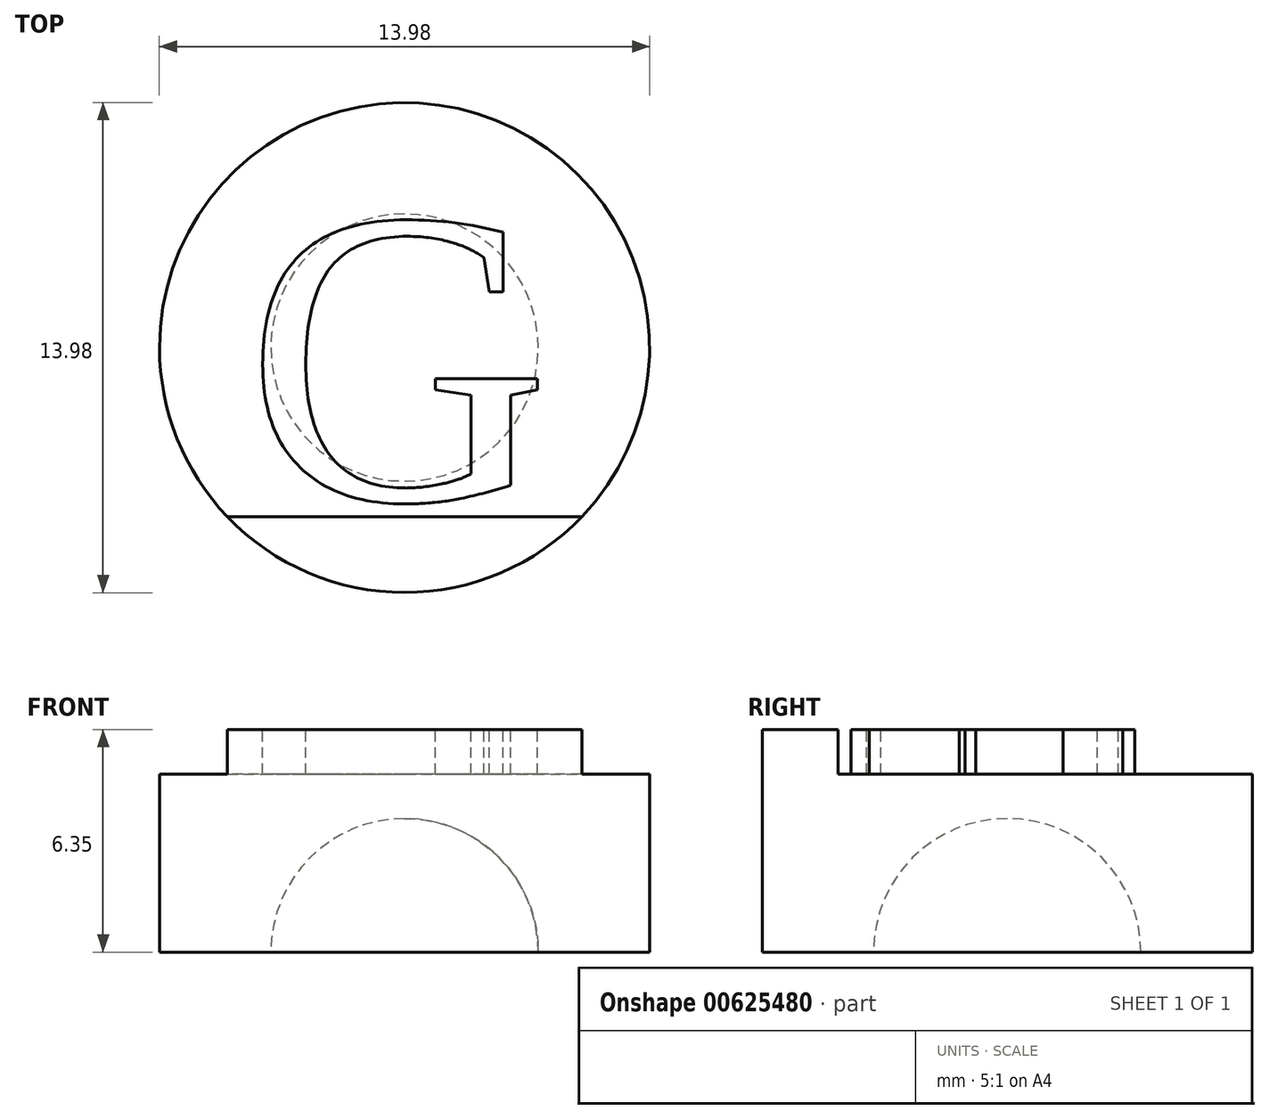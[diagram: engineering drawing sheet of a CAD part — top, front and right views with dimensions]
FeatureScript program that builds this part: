
annotation { "Feature Type Name" : "Feature", "Feature Type Description" : "" }
export const myFeature = defineFeature(function(context is Context, id is Id, definition is map)
    precondition{}
    {
        {
            var Q0;
            Q0=qCreatedBy(makeId("Front.planeOp"),FACE);
            var sketch = newSketch(context, id + "F0", { "sketchPlane" : qUnion([Q0])});
            skLineSegment(sketch, "E0", {"start": v(-6.99, 0) * mm, "end": v(-3.8, 0) * mm});
            skLineSegment(sketch, "E1", {"start": v(0, 3.81) * mm, "end": v(0, 6.35) * mm});
            skLineSegment(sketch, "E2", {"start": v(0, 6.35) * mm, "end": v(-6.99, 6.35) * mm});
            skLineSegment(sketch, "E3", {"start": v(-6.99, 6.35) * mm, "end": v(-6.99, 0) * mm});
            skArc(sketch, "E4", {"start": v(0, 3.81) * mm, "mid": v(-2.7, 2.7) * mm, "end": v(-3.81, 0) * mm});
            skSolve(sketch);
        }
        {
            var Q0;
            Q0 = qSketchRegion(id + "F0", true);
            var Q1;
            Q1=sQuery(id+"F0.wireOp",EDGE,"E1");
            revolve(context, id + "F1", {"entities" : qUnion([Q0]), "axis" : qUnion([Q1]), "revolveType" : RevolveType.FULL});
        }
        {
            var Q0;
            Q0=makeQuery(id+"F1.opRevolve","SWEPT_FACE",FACE,{"disambiguationData":[OSD([sQuery(id+"F0.wireOp",EDGE,"E2")])]});
            var sketch = newSketch(context, id + "F2", { "sketchPlane" : qUnion([Q0])});
            skLineSegment(sketch, "E5.bottom", {"start": v(5.05, 4.83) * mm, "end": v(-5.05, 4.83) * mm});
            skLineSegment(sketch, "E5.top", {"start": v(5.05, -4.83) * mm, "end": v(-5.05, -4.83) * mm});
            skLineSegment(sketch, "E5.left", {"start": v(5.05, 4.83) * mm, "end": v(5.05, -4.83) * mm});
            skLineSegment(sketch, "E5.right", {"start": v(-5.05, 4.83) * mm, "end": v(-5.05, -4.83) * mm});
            skPoint(sketch, "E5.middle", {"position": v(0, 0) * mm});
            skText(sketch, "E6", { "text": "G", "fontName": "Tinos-Regular.ttf"});
            const initialGuessF2  = {"E6": [-0.00454, -0.00434, 1, 0, 0.00868]};
            skSetInitialGuess(sketch, initialGuessF2);
            skSolve(sketch);
        }
        {
            var Q0;
            {var subQ0=sQuery(id+"F2.wireOp",EDGE,"E5.bottom");Q0=makeQuery(id+"F2.imprint","IMPRINT",FACE,{"disambiguationData":[TD([[makeQuery(id+"F2.imprint","IMPRINT",EDGE,{"derivedFrom":subQ0}),-1.0]])]});}
            var Q1;
            Q1=makeQuery(id+"F2.imprint","IMPRINT",FACE,{"disambiguationData":[TD([[makeQuery(id+"F2.imprint","IMPRINT",EDGE,{"derivedFrom":sQuery(id+"F2.wireOp",EDGE,"E5.bottom")}),1.0]])]});
            var Q2;
            {var subQ0=sQuery(id+"F2.wireOp",EDGE,"E5.right");Q2=makeQuery(id+"F2.imprint","IMPRINT",FACE,{"disambiguationData":[TD([[makeQuery(id+"F2.imprint","IMPRINT",EDGE,{"derivedFrom":subQ0}),-1.0]])]});}
            var Q3;
            {var subQ0=sQuery(id+"F2.wireOp",EDGE,"E6.sketch_text.stroke-2");var subQ1=sQuery(id+"F2.wireOp",EDGE,"E6.sketch_text.stroke-1");var subQ2=makeQuery(id+"F2.imprint","INTERSECT",VERTEX,{"derivedFrom":[subQ1,subQ0]});Q3=makeQuery(id+"F2.imprint","IMPRINT",FACE,{"disambiguationData":[TD([[makeQuery(id+"F2.imprint","IMPRINT",EDGE,{"disambiguationData":[TD([[subQ2,1.0]])],"derivedFrom":subQ1}),1.0]])]});}
            var Q4;
            {var subQ0=sQuery(id+"F2.wireOp",EDGE,"E5.left");Q4=makeQuery(id+"F2.imprint","IMPRINT",FACE,{"disambiguationData":[TD([[makeQuery(id+"F2.imprint","IMPRINT",EDGE,{"derivedFrom":subQ0}),1.0]])]});}
            extrude(context, id + "F3", {"entities" : qUnion([Q0, Q1, Q2, Q3, Q4]), "operationType" : NewBodyOperationType.REMOVE, "oppositeDirection" : true, "depth" : 1.27 * mm, "offsetDistance" : 25.4 * mm});
        }
    });
